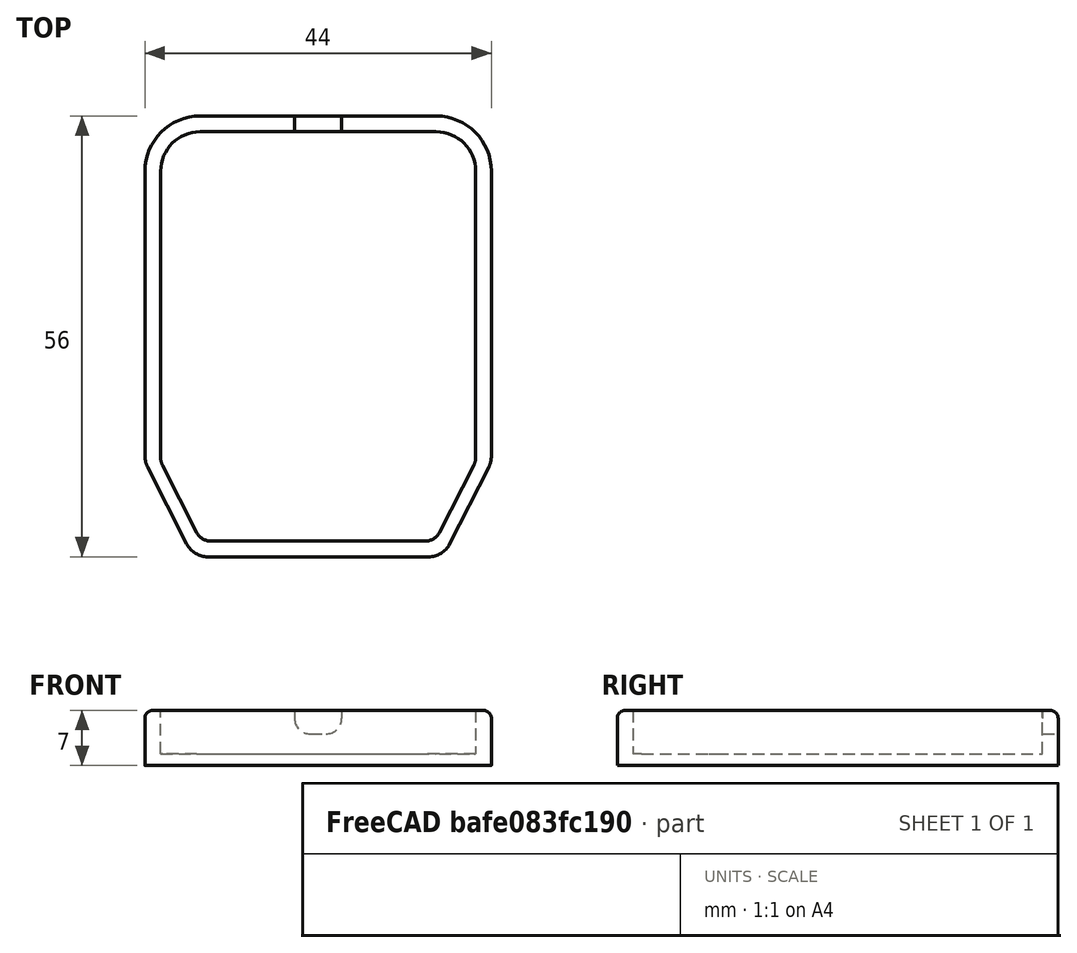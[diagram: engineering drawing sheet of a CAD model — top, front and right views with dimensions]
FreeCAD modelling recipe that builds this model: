
FCSTD DOCUMENT  (FreeCAD 0.15R4671 (Git))
Label: hardware
License: CreativeCommons Attribution-ShareAlike
LicenseURL: http://creativecommons.org/licenses/by-sa/4.0/
objects: Part::Fillet×8, Part::Box×7, Part::Cut×6
note: 21 computed .brp shape members not serialized (recipe doc carries the construction recipe); baked Part::Feature solids carry a one-line shape summary decoded from their .brp

FEATURE [Part::Box] Box  label="Cube"
  Height = 10
  Length = 40
  Width = 52
FEATURE [Part::Box] Box001  label="Cube001"
  Height = 10
  Length = 10
  Placement = pos=(-1,-10,0) rot=(0,0,1;0.471239rad)
  Width = 100
FEATURE [Part::Box] Box002  label="Cube002"
  Height = 10
  Length = 10
  Placement = pos=(30,-9.5,0) rot=(0,0,-1;0.471239rad)
  Width = 100
FEATURE [Part::Fillet] Fillet
  Base = -> Box
  Edges = 2 edges r=5: [Edge3,Edge7]
FEATURE [Part::Cut] Cut
  Base = -> Fillet
  Tool = -> Box001
FEATURE [Part::Cut] Cut001
  Base = -> Cut
  Tool = -> Box002
FEATURE [Part::Fillet] Fillet001
  Base = -> Cut001
  Edges = 2 edges r=2: [Edge20,Edge24]
FEATURE [Part::Fillet] Fillet002  label="GPS Profile"
  Base = -> Fillet001
  Edges = 2 edges r=2: [Edge12,Edge26]
  Placement = pos=(0,0,1.5) rot=(0,0,1;0rad)
FEATURE [Part::Box] Box003  label="Cube003"
  Height = 7
  Length = 44
  Placement = pos=(-2,-2,0) rot=(0,0,1;0rad)
  Width = 56
FEATURE [Part::Box] Box004  label="Cube004"
  Height = 10
  Length = 10
  Placement = pos=(30,-13.5,0) rot=(0,0,-1;0.471239rad)
  Width = 100
FEATURE [Part::Box] Box005  label="Cube005"
  Height = 10
  Length = 10
  Placement = pos=(-3,-10,0) rot=(0,0,1;0.471239rad)
  Width = 100
FEATURE [Part::Fillet] Fillet003
  Base = -> Box003
  Edges = 2 edges r=7: [Edge3,Edge7]
FEATURE [Part::Cut] Cut002
  Base = -> Fillet003
  Tool = -> Box004
FEATURE [Part::Cut] Cut003
  Base = -> Cut002
  Tool = -> Box005
FEATURE [Part::Fillet] Fillet004
  Base = -> Cut003
  Edges = 2 edges r=3: [Edge20,Edge24]
FEATURE [Part::Fillet] Fillet005
  Base = -> Fillet004
  Edges = 2 edges r=3: [Edge12,Edge26]
FEATURE [Part::Cut] Cut004
  Base = -> Fillet005
  Tool = -> Fillet002
FEATURE [Part::Fillet] Fillet006
  Base = -> Cut004
  Edges = 12 edges r=1: [Edge1,Edge2,Edge3,Edge4,Edge5,Edge6,Edge7,Edge8,Edge9,Edge10,Edge11,Edge12]
FEATURE [Part::Box] Box006  label="Cube006"
  Height = 10
  Length = 6
  Placement = pos=(17,30,0) rot=(0,0,1;0rad)
  Width = 30
FEATURE [Part::Fillet] Fillet007
  Base = -> Box006
  Edges = 2 edges r=2: [Edge4,Edge8]
  Placement = pos=(0,0,4) rot=(0,0,1;0rad)
FEATURE [Part::Cut] Cut005  label="gps-mount"
  Base = -> Fillet006
  Tool = -> Fillet007
